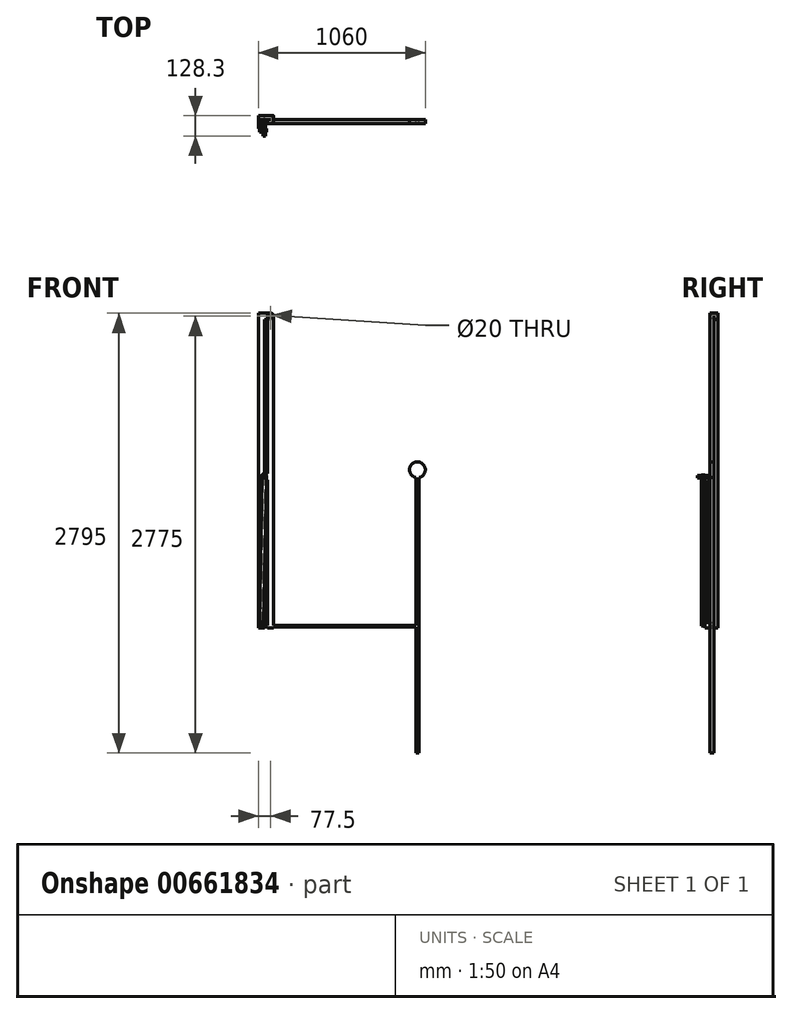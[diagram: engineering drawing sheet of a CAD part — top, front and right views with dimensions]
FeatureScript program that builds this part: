
annotation { "Feature Type Name" : "Feature", "Feature Type Description" : "" }
export const myFeature = defineFeature(function(context is Context, id is Id, definition is map)
    precondition{}
    {
        {
            var Q0;
            Q0=qCreatedBy(makeId("Front.planeOp"),FACE);
            var sketch = newSketch(context, id + "F0", { "sketchPlane" : qUnion([Q0])});
            skLineSegment(sketch, "E0.bottom", {"start": v(20, 1000) * mm, "end": v(-20, 1000) * mm});
            skLineSegment(sketch, "E0.top", {"start": v(20, -1000) * mm, "end": v(-20, -1000) * mm});
            skLineSegment(sketch, "E0.left", {"start": v(20, 1000) * mm, "end": v(20, -1000) * mm});
            skLineSegment(sketch, "E0.right", {"start": v(-20, 1000) * mm, "end": v(-20, -1000) * mm});
            skPoint(sketch, "E0.middle", {"position": v(0, 0) * mm});
            skLineSegment(sketch, "E1.bottom", {"start": v(20, 1000) * mm, "end": v(95, 1000) * mm});
            skLineSegment(sketch, "E1.top", {"start": v(20, 960) * mm, "end": v(95, 960) * mm});
            skLineSegment(sketch, "E1.left", {"start": v(20, 1000) * mm, "end": v(20, 960) * mm});
            skLineSegment(sketch, "E1.right", {"start": v(95, 1000) * mm, "end": v(95, 960) * mm});
            skCircle(sketch, "E2", {"center": v(57.5, 980) * mm, "radius": 20 * mm});
            skPoint(sketch, "E2.centerSnap0", {"position": v(57.5, 960) * mm});
            skPoint(sketch, "E2.centerSnap1", {"position": v(95, 980) * mm});
            skCircle(sketch, "E3", {"center": v(57.5, 980) * mm, "radius": 10 * mm});
            skSolve(sketch);
        }
        {
            var Q0;
            {var subQ1=sQuery(id+"F0.wireOp",EDGE,"E0.bottom");Q0=makeQuery(id+"F0.imprint","IMPRINT",FACE,{"disambiguationData":[TD([[makeQuery(id+"F0.imprint","IMPRINT",EDGE,{"derivedFrom":subQ1}),1.0]])]});}
            var Q1;
            {var subQ0=sQuery(id+"F0.wireOp",EDGE,"E1.bottom");var subQ3=sQuery(id+"F0.wireOp",EDGE,"E2");var subQ5=makeQuery(id+"F0.imprint","INTERSECT",VERTEX,{"derivedFrom":[subQ0,subQ3]});Q1=makeQuery(id+"F0.imprint","IMPRINT",FACE,{"disambiguationData":[TD([[makeQuery(id+"F0.imprint","IMPRINT",EDGE,{"disambiguationData":[TD([[subQ5,-1.0]])],"derivedFrom":subQ3}),-1.0]])]});}
            var Q2;
            Q2=makeQuery(id+"F0.imprint","IMPRINT",FACE,{"disambiguationData":[TD([[makeQuery(id+"F0.imprint","IMPRINT",EDGE,{"derivedFrom":sQuery(id+"F0.wireOp",EDGE,"E3")}),-1.0]])]});
            var Q3;
            {var subQ0=sQuery(id+"F0.wireOp",EDGE,"E1.top");var subQ1=sQuery(id+"F0.wireOp",EDGE,"E0.left");var subQ2=makeQuery(id+"F0.imprint","INTERSECT",VERTEX,{"derivedFrom":[subQ1,subQ0]});Q3=makeQuery(id+"F0.imprint","IMPRINT",FACE,{"disambiguationData":[TD([[makeQuery(id+"F0.imprint","IMPRINT",EDGE,{"disambiguationData":[TD([[subQ2,1.0]])],"derivedFrom":subQ1}),1.0]])]});}
            extrude(context, id + "F1", {"entities" : qUnion([Q0, Q1, Q2, Q3]), "depth" : 25 * mm, "offsetDistance" : 25 * mm});
        }
        {
            var Q0;
            Q0=makeQuery(id+"F1.opExtrude","CAP_FACE",FACE,{"disambiguationData":[OSD([sQuery(id+"F0.wireOp",EDGE,"E0.bottom"),sQuery(id+"F0.wireOp",EDGE,"E0.top"),sQuery(id+"F0.wireOp",EDGE,"E0.left"),sQuery(id+"F0.wireOp",EDGE,"E0.right"),sQuery(id+"F0.wireOp",EDGE,"E1.bottom"),sQuery(id+"F0.wireOp",EDGE,"E1.top"),sQuery(id+"F0.wireOp",EDGE,"E2"),sQuery(id+"F0.wireOp",EDGE,"E3")])],"isStart":false});
            var sketch = newSketch(context, id + "F2", { "sketchPlane" : qUnion([Q0])});
            skCircle(sketch, "E4.0", {"center": v(57.5, 980) * mm, "radius": 10 * mm});
            skLineSegment(sketch, "E5.bottom", {"start": v(37.5, 1000) * mm, "end": v(77.5, 1000) * mm});
            skLineSegment(sketch, "E5.top", {"start": v(37.5, -1000) * mm, "end": v(77.5, -1000) * mm});
            skLineSegment(sketch, "E5.left", {"start": v(37.5, 1000) * mm, "end": v(37.5, -1000) * mm});
            skLineSegment(sketch, "E5.right", {"start": v(77.5, 1000) * mm, "end": v(77.5, -1000) * mm});
            skCircle(sketch, "E6", {"center": v(57.5, 980) * mm, "radius": 20 * mm});
            skPoint(sketch, "E6.centerSnap0", {"position": v(57.5, 1000) * mm});
            skSolve(sketch);
        }
        {
            var Q0;
            {var subQ6=sQuery(id+"F2.wireOp",EDGE,"E5.top");Q0=makeQuery(id+"F2.imprint","IMPRINT",FACE,{"disambiguationData":[TD([[makeQuery(id+"F2.imprint","IMPRINT",EDGE,{"derivedFrom":subQ6}),1.0]])]});}
            var Q1;
            Q1=makeQuery(id+"F2.imprint","IMPRINT",FACE,{"disambiguationData":[TD([[makeQuery(id+"F2.imprint","IMPRINT",EDGE,{"derivedFrom":sQuery(id+"F2.wireOp",EDGE,"E4.0")}),-1.0]])]});
            var Q2;
            {var subQ0=sQuery(id+"F2.wireOp",EDGE,"E6");var subQ1=sQuery(id+"F2.wireOp",EDGE,"E5.left");var subQ2=makeQuery(id+"F2.imprint","INTERSECT",VERTEX,{"derivedFrom":[subQ1,subQ0]});Q2=makeQuery(id+"F2.imprint","IMPRINT",FACE,{"disambiguationData":[TD([[makeQuery(id+"F2.imprint","IMPRINT",EDGE,{"disambiguationData":[TD([[subQ2,-1.0]])],"derivedFrom":subQ1}),1.0]])]});}
            extrude(context, id + "F3", {"entities" : qUnion([Q0, Q1, Q2]), "depth" : 25 * mm, "offsetDistance" : 25 * mm});
        }
        {
            var Q0;
            Q0=makeQuery(id+"F1.opExtrude","CAP_FACE",FACE,{"disambiguationData":[OSD([sQuery(id+"F0.wireOp",EDGE,"E0.bottom"),sQuery(id+"F0.wireOp",EDGE,"E0.top"),sQuery(id+"F0.wireOp",EDGE,"E0.left"),sQuery(id+"F0.wireOp",EDGE,"E0.right"),sQuery(id+"F0.wireOp",EDGE,"E1.bottom"),sQuery(id+"F0.wireOp",EDGE,"E1.top"),sQuery(id+"F0.wireOp",EDGE,"E2"),sQuery(id+"F0.wireOp",EDGE,"E3")])],"isStart":false});
            var sketch = newSketch(context, id + "F4", { "sketchPlane" : qUnion([Q0])});
            skLineSegment(sketch, "E7", {"start": v(20, -985) * mm, "end": v(-20, -985) * mm});
            skLineSegment(sketch, "E8", {"start": v(-20, -1000) * mm, "end": v(20, -1000) * mm});
            skLineSegment(sketch, "E9", {"start": v(20, -1000) * mm, "end": v(20, -985) * mm});
            skSolve(sketch);
        }
        {
            var Q0;
            Q0=makeQuery(id+"F4.imprint","IMPRINT",FACE,{"disambiguationData":[TD([[makeQuery(id+"F4.imprint","IMPRINT",EDGE,{"derivedFrom":sQuery(id+"F4.wireOp",EDGE,"E7")}),1.0]])]});
            extrude(context, id + "F5", {"entities" : qUnion([Q0]), "operationType" : NewBodyOperationType.ADD, "depth" : 55 * mm, "offsetDistance" : 25 * mm});
        }
        {
            var Q0;
            Q0=makeQuery(id+"F3.opExtrude","SWEPT_FACE",FACE,{"disambiguationData":[OSD([sQuery(id+"F2.wireOp",EDGE,"E5.left")])]});
            var sketch = newSketch(context, id + "F6", { "sketchPlane" : qUnion([Q0])});
            skLineSegment(sketch, "E10.bottom", {"start": v(50, -60) * mm, "end": v(46, -60) * mm});
            skLineSegment(sketch, "E10.top", {"start": v(50, -20) * mm, "end": v(46, -20) * mm});
            skLineSegment(sketch, "E10.left", {"start": v(50, -60) * mm, "end": v(50, -20) * mm});
            skLineSegment(sketch, "E10.right", {"start": v(46, -60) * mm, "end": v(46, -20) * mm});
            skSolve(sketch);
        }
        {
            var Q0;
            Q0 = qSketchRegion(id + "F6", true);
            extrude(context, id + "F7", {"entities" : qUnion([Q0]), "operationType" : NewBodyOperationType.ADD, "depth" : 40 * mm, "offsetDistance" : 25 * mm});
        }
        {
            var Q0;
            Q0=makeQuery(id+"F7.boolean.opBoolean","MERGE",FACE,{"derivedFrom":[makeQuery(id+"F3.opExtrude","CAP_FACE",FACE,{"disambiguationData":[OSD([sQuery(id+"F2.wireOp",EDGE,"E4.0"),sQuery(id+"F2.wireOp",EDGE,"E5.top"),sQuery(id+"F2.wireOp",EDGE,"E5.left"),sQuery(id+"F2.wireOp",EDGE,"E5.right"),sQuery(id+"F2.wireOp",EDGE,"E6")])],"isStart":false}),makeQuery(id+"F7.opExtrude","SWEPT_FACE",FACE,{"disambiguationData":[OSD([sQuery(id+"F6.wireOp",EDGE,"E10.left")])]})]});
            var sketch = newSketch(context, id + "F8", { "sketchPlane" : qUnion([Q0])});
            skCircle(sketch, "E11", {"center": v(17.5, -40) * mm, "radius": 20 * mm});
            skPoint(sketch, "E11.centerSnap0", {"position": v(17.5, -60) * mm});
            skPoint(sketch, "E11.centerSnap1", {"position": v(-2.5, -40) * mm});
            skCircle(sketch, "E12", {"center": v(17.5, -40) * mm, "radius": 7.5 * mm});
            skSolve(sketch);
        }
        {
            var Q0;
            {var subQ0=sQuery(id+"F8.wireOp",EDGE,"E11");var subQ1=sQuery(id+"F6.wireOp",EDGE,"E10.left");var subQ2=makeQuery(id+"F7.opExtrude","CAP_EDGE",EDGE,{"disambiguationData":[OSD([subQ1])],"isStart":false});var subQ3=makeQuery(id+"F8.imprint","INTERSECT",VERTEX,{"derivedFrom":[subQ2,subQ0]});Q0=makeQuery(id+"F8.imprint","IMPRINT",FACE,{"disambiguationData":[TD([[makeQuery(id+"F8.imprint","IMPRINT",EDGE,{"disambiguationData":[TD([[subQ3,1.0]])],"derivedFrom":subQ0}),-1.0]])]});}
            var Q1;
            {var subQ0=sQuery(id+"F8.wireOp",EDGE,"E11");var subQ1=sQuery(id+"F6.wireOp",EDGE,"E10.left");var subQ2=makeQuery(id+"F7.opExtrude","CAP_EDGE",EDGE,{"disambiguationData":[OSD([subQ1])],"isStart":false});var subQ3=makeQuery(id+"F8.imprint","INTERSECT",VERTEX,{"derivedFrom":[subQ2,subQ0]});Q1=makeQuery(id+"F8.imprint","IMPRINT",FACE,{"disambiguationData":[TD([[makeQuery(id+"F8.imprint","IMPRINT",EDGE,{"disambiguationData":[TD([[subQ3,-1.0]])],"derivedFrom":subQ0}),-1.0]])]});}
            extrude(context, id + "F9", {"entities" : qUnion([Q0, Q1]), "operationType" : NewBodyOperationType.REMOVE, "oppositeDirection" : true, "depth" : 5 * mm, "offsetDistance" : 25 * mm});
        }
        {
            var Q0;
            Q0=makeQuery(id+"F5.opExtrude","SWEPT_FACE",FACE,{"disambiguationData":[OSD([sQuery(id+"F4.wireOp",EDGE,"E7")])]});
            var sketch = newSketch(context, id + "F10", { "sketchPlane" : qUnion([Q0])});
            skLineSegment(sketch, "E13", {"start": v(20, -52.5) * mm, "end": v(-20, -52.5) * mm, "construction": true});
            skLineSegment(sketch, "E14", {"start": v(0, -80) * mm, "end": v(0, -25) * mm, "construction": true});
            skCircle(sketch, "E15", {"center": v(0, -52.5) * mm, "radius": 7.5 * mm});
            skSolve(sketch);
        }
        {
            var Q0;
            Q0 = qSketchRegion(id + "F10", true);
            extrude(context, id + "F11", {"entities" : qUnion([Q0]), "operationType" : NewBodyOperationType.ADD, "depth" : 919 * mm, "offsetDistance" : 25 * mm});
        }
        {
            var Q0;
            Q0=makeQuery(id+"F5.opExtrude","SWEPT_FACE",FACE,{"disambiguationData":[OSD([sQuery(id+"F4.wireOp",EDGE,"E7")])]});
            extrude(context, id + "F12", {"entities" : qUnion([Q0]), "depth" : 20 * mm, "offsetDistance" : 25 * mm});
        }
        {
            var Q0;
            {var subQ0=sQuery(id+"F4.wireOp",EDGE,"E7");Q0=makeQuery(id+"F12.opExtrude","SWEPT_FACE",FACE,{"disambiguationData":[OSD([subQ0]),TDD([makeQuery(id+"F5.opExtrude","CAP_EDGE",EDGE,{"disambiguationData":[OSD([subQ0])],"isStart":false})])]});}
            var sketch = newSketch(context, id + "F13", { "sketchPlane" : qUnion([Q0])});
            skCircle(sketch, "E16", {"center": v(0, -975) * mm, "radius": 5 * mm});
            skPoint(sketch, "E16.centerSnap0", {"position": v(-20, -975) * mm});
            skPoint(sketch, "E16.centerSnap1", {"position": v(0, -965) * mm});
            skSolve(sketch);
        }
        {
            var Q0;
            Q0=makeQuery(id+"F13.imprint","IMPRINT",FACE,{"disambiguationData":[TD([[makeQuery(id+"F13.imprint","IMPRINT",EDGE,{"derivedFrom":sQuery(id+"F13.wireOp",EDGE,"E16")}),-1.0]])]});
            var sketch = newSketch(context, id + "F14", { "sketchPlane" : qUnion([Q0])});
            skCircle(sketch, "E17.0", {"center": v(0, -975) * mm, "radius": 5 * mm});
            skCircle(sketch, "E18.0", {"center": v(17.5, -40) * mm, "radius": 7.5 * mm});
            skLineSegment(sketch, "E19", {"start": v(30.99, -27) * mm, "end": v(13, -988.49) * mm});
            skLineSegment(sketch, "E20", {"start": v(13, -988.49) * mm, "end": v(-13.49, -988) * mm});
            skLineSegment(sketch, "E21", {"start": v(-13.49, -988) * mm, "end": v(4.5, -26.51) * mm});
            skLineSegment(sketch, "E22", {"start": v(4.5, -26.51) * mm, "end": v(30.99, -27) * mm});
            skLineSegment(sketch, "E23", {"start": v(17.5, -40) * mm, "end": v(0, -975) * mm, "construction": true});
            skCircle(sketch, "E24", {"center": v(0, -975) * mm, "radius": 13.24 * mm});
            skCircle(sketch, "E25", {"center": v(17.5, -40) * mm, "radius": 13.24 * mm});
            skSolve(sketch);
        }
        {
            var Q0;
            {var subQ0=sQuery(id+"F14.wireOp",EDGE,"E24");var subQ1=sQuery(id+"F4.wireOp",EDGE,"E7");var subQ2=makeQuery(id+"F13.imprint","IMPRINT",EDGE,{"derivedFrom":makeQuery(id+"F12.opExtrude","CAP_EDGE",EDGE,{"disambiguationData":[OSD([subQ1]),TDD([makeQuery(id+"F5.opExtrude","CAP_EDGE",EDGE,{"disambiguationData":[OSD([subQ1])],"isStart":false})])],"isStart":false})});var subQ3=makeQuery(id+"F14.imprint","INTERSECT",VERTEX,{"disambiguationData":[OD(0.0)],"derivedFrom":[subQ2,subQ0]});Q0=makeQuery(id+"F14.imprint","IMPRINT",FACE,{"disambiguationData":[TD([[makeQuery(id+"F14.imprint","IMPRINT",EDGE,{"disambiguationData":[TD([[subQ3,1.0]])],"derivedFrom":subQ0}),1.0]])]});}
            var Q1;
            {var subQ0=sQuery(id+"F14.wireOp",EDGE,"E24");var subQ1=sQuery(id+"F14.wireOp",EDGE,"E19");var subQ2=makeQuery(id+"F14.imprint","INTERSECT",VERTEX,{"derivedFrom":[subQ1,subQ0]});Q1=makeQuery(id+"F14.imprint","IMPRINT",FACE,{"disambiguationData":[TD([[makeQuery(id+"F14.imprint","IMPRINT",EDGE,{"disambiguationData":[TD([[subQ2,1.0]])],"derivedFrom":subQ1}),-1.0]])]});}
            var Q2;
            {var subQ0=sQuery(id+"F14.wireOp",EDGE,"E24");var subQ1=sQuery(id+"F14.wireOp",EDGE,"E21");var subQ2=makeQuery(id+"F14.imprint","INTERSECT",VERTEX,{"derivedFrom":[subQ1,subQ0]});Q2=makeQuery(id+"F14.imprint","IMPRINT",FACE,{"disambiguationData":[TD([[makeQuery(id+"F14.imprint","IMPRINT",EDGE,{"disambiguationData":[TD([[subQ2,-1.0]])],"derivedFrom":subQ1}),-1.0]])]});}
            var Q3;
            {var subQ0=sQuery(id+"F14.wireOp",EDGE,"E24");var subQ1=makeQuery(id+"F14.imprint","INTERSECT",VERTEX,{"derivedFrom":[sQuery(id+"F14.wireOp",EDGE,"E20"),subQ0]});Q3=makeQuery(id+"F14.imprint","IMPRINT",FACE,{"disambiguationData":[TD([[makeQuery(id+"F14.imprint","IMPRINT",EDGE,{"disambiguationData":[TD([[subQ1,1.0]])],"derivedFrom":subQ0}),1.0]])]});}
            var Q4;
            {var subQ0=sQuery(id+"F14.wireOp",EDGE,"E25");var subQ1=sQuery(id+"F14.wireOp",EDGE,"E19");var subQ2=makeQuery(id+"F14.imprint","INTERSECT",VERTEX,{"derivedFrom":[subQ1,subQ0]});Q4=makeQuery(id+"F14.imprint","IMPRINT",FACE,{"disambiguationData":[TD([[makeQuery(id+"F14.imprint","IMPRINT",EDGE,{"disambiguationData":[TD([[subQ2,1.0]])],"derivedFrom":subQ0}),-1.0]])]});}
            var Q5;
            Q5=makeQuery(id+"F14.imprint","IMPRINT",FACE,{"disambiguationData":[TD([[makeQuery(id+"F14.imprint","IMPRINT",EDGE,{"derivedFrom":sQuery(id+"F14.wireOp",EDGE,"E17.0")}),-1.0]])]});
            var Q6;
            Q6=makeQuery(id+"F14.imprint","IMPRINT",FACE,{"disambiguationData":[TD([[makeQuery(id+"F14.imprint","IMPRINT",EDGE,{"derivedFrom":sQuery(id+"F14.wireOp",EDGE,"E18.0")}),-1.0]])]});
            extrude(context, id + "F15", {"entities" : qUnion([Q0, Q1, Q2, Q3, Q4, Q5, Q6]), "depth" : 25 * mm, "offsetDistance" : 25 * mm});
        }
        {
            var Q0;
            Q0=makeQuery(id+"F13.imprint","IMPRINT",FACE,{"disambiguationData":[TD([[makeQuery(id+"F13.imprint","IMPRINT",EDGE,{"derivedFrom":sQuery(id+"F13.wireOp",EDGE,"E16")}),1.0]])]});
            extrude(context, id + "F16", {"entities" : qUnion([Q0]), "operationType" : NewBodyOperationType.ADD, "depth" : 25 * mm, "offsetDistance" : 25 * mm});
        }
        {
            var Q0;
            Q0=makeQuery(id+"F8.imprint","IMPRINT",FACE,{"disambiguationData":[TD([[makeQuery(id+"F8.imprint","IMPRINT",EDGE,{"derivedFrom":sQuery(id+"F8.wireOp",EDGE,"E12")}),1.0]])]});
            extrude(context, id + "F17", {"entities" : qUnion([Q0]), "operationType" : NewBodyOperationType.ADD, "depth" : 78.3 * mm, "offsetDistance" : 25 * mm});
        }
        {
            var Q0;
            Q0=makeQuery(id+"F1.opExtrude","CAP_FACE",FACE,{"disambiguationData":[OSD([sQuery(id+"F0.wireOp",EDGE,"E0.bottom"),sQuery(id+"F0.wireOp",EDGE,"E0.top"),sQuery(id+"F0.wireOp",EDGE,"E0.left"),sQuery(id+"F0.wireOp",EDGE,"E0.right"),sQuery(id+"F0.wireOp",EDGE,"E1.bottom"),sQuery(id+"F0.wireOp",EDGE,"E1.top"),sQuery(id+"F0.wireOp",EDGE,"E2"),sQuery(id+"F0.wireOp",EDGE,"E3")])],"isStart":false});
            var sketch = newSketch(context, id + "F18", { "sketchPlane" : qUnion([Q0])});
            skLineSegment(sketch, "E26.bottom", {"start": v(-20, -985) * mm, "end": v(980, -985) * mm});
            skLineSegment(sketch, "E26.top", {"start": v(-20, -995) * mm, "end": v(980, -995) * mm});
            skLineSegment(sketch, "E26.left", {"start": v(-20, -985) * mm, "end": v(-20, -995) * mm});
            skLineSegment(sketch, "E26.right", {"start": v(980, -985) * mm, "end": v(980, -995) * mm});
            skLineSegment(sketch, "E27.bottom", {"start": v(1000, -985) * mm, "end": v(980, -985) * mm});
            skLineSegment(sketch, "E27.top", {"start": v(1000, 5) * mm, "end": v(980, 5) * mm});
            skLineSegment(sketch, "E27.left", {"start": v(1000, -985) * mm, "end": v(1000, 5) * mm});
            skLineSegment(sketch, "E27.right", {"start": v(980, -985) * mm, "end": v(980, 5) * mm});
            skCircle(sketch, "E28", {"center": v(990, 5) * mm, "radius": 50 * mm});
            skLineSegment(sketch, "E29.bottom", {"start": v(980, -995) * mm, "end": v(1000, -995) * mm});
            skLineSegment(sketch, "E29.top", {"start": v(980, -1795) * mm, "end": v(1000, -1795) * mm});
            skLineSegment(sketch, "E29.left", {"start": v(980, -995) * mm, "end": v(980, -1795) * mm});
            skLineSegment(sketch, "E29.right", {"start": v(1000, -995) * mm, "end": v(1000, -1795) * mm});
            skLineSegment(sketch, "E30", {"start": v(1000, -985) * mm, "end": v(1000, -995) * mm});
            skSolve(sketch);
        }
        {
            var Q0;
            Q0 = qSketchRegion(id + "F18", true);
            extrude(context, id + "F19", {"entities" : qUnion([Q0]), "operationType" : NewBodyOperationType.ADD, "depth" : 25 * mm, "offsetDistance" : 25 * mm});
        }
    });
